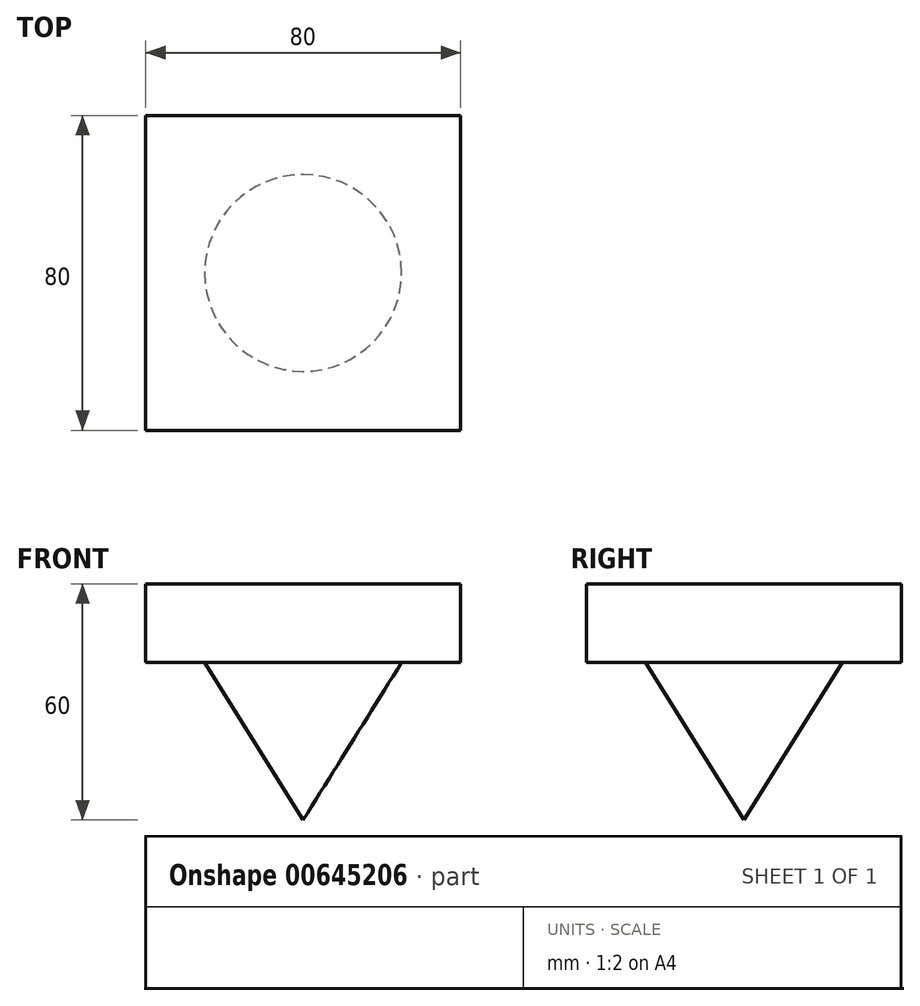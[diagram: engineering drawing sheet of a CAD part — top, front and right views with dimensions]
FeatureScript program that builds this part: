
annotation { "Feature Type Name" : "Feature", "Feature Type Description" : "" }
export const myFeature = defineFeature(function(context is Context, id is Id, definition is map)
    precondition{}
    {
        {
            var Q0;
            Q0=qCreatedBy(makeId("Top.planeOp"),FACE);
            var sketch = newSketch(context, id + "F0", { "sketchPlane" : qUnion([Q0])});
            skLineSegment(sketch, "E0.bottom", {"start": v(40, -40) * mm, "end": v(-40, -40) * mm});
            skLineSegment(sketch, "E0.top", {"start": v(40, 40) * mm, "end": v(-40, 40) * mm});
            skLineSegment(sketch, "E0.left", {"start": v(40, -40) * mm, "end": v(40, 40) * mm});
            skLineSegment(sketch, "E0.right", {"start": v(-40, -40) * mm, "end": v(-40, 40) * mm});
            skPoint(sketch, "E0.middle", {"position": v(0, 0) * mm});
            skSolve(sketch);
        }
        {
            var Q0;
            Q0=makeQuery(id+"F0.imprint","IMPRINT",FACE,{"disambiguationData":[TD([[makeQuery(id+"F0.imprint","IMPRINT",EDGE,{"derivedFrom":sQuery(id+"F0.wireOp",EDGE,"E0.bottom")}),-1.0]])]});
            extrude(context, id + "F1", {"entities" : qUnion([Q0]), "depth" : 20 * mm, "offsetDistance" : 25.4 * mm});
        }
        {
            var Q0;
            Q0=qCreatedBy(makeId("Front.planeOp"),FACE);
            var sketch = newSketch(context, id + "F2", { "sketchPlane" : qUnion([Q0])});
            skLineSegment(sketch, "E1", {"start": v(0, 0) * mm, "end": v(0, -40) * mm});
            skLineSegment(sketch, "E2", {"start": v(0, 0) * mm, "end": v(25, 0) * mm});
            skLineSegment(sketch, "E3", {"start": v(0, -40) * mm, "end": v(25, 0) * mm});
            skSolve(sketch);
        }
        {
            var Q0;
            Q0=makeQuery(id+"F2.imprint","IMPRINT",FACE,{"disambiguationData":[TD([[makeQuery(id+"F2.imprint","IMPRINT",EDGE,{"derivedFrom":sQuery(id+"F2.wireOp",EDGE,"E1")}),1.0]])]});
            var Q1;
            Q1=sQuery(id+"F2.wireOp",EDGE,"E1");
            revolve(context, id + "F3", {"operationType" : NewBodyOperationType.ADD, "entities" : qUnion([Q0]), "axis" : qUnion([Q1]), "revolveType" : RevolveType.FULL});
        }
    });
